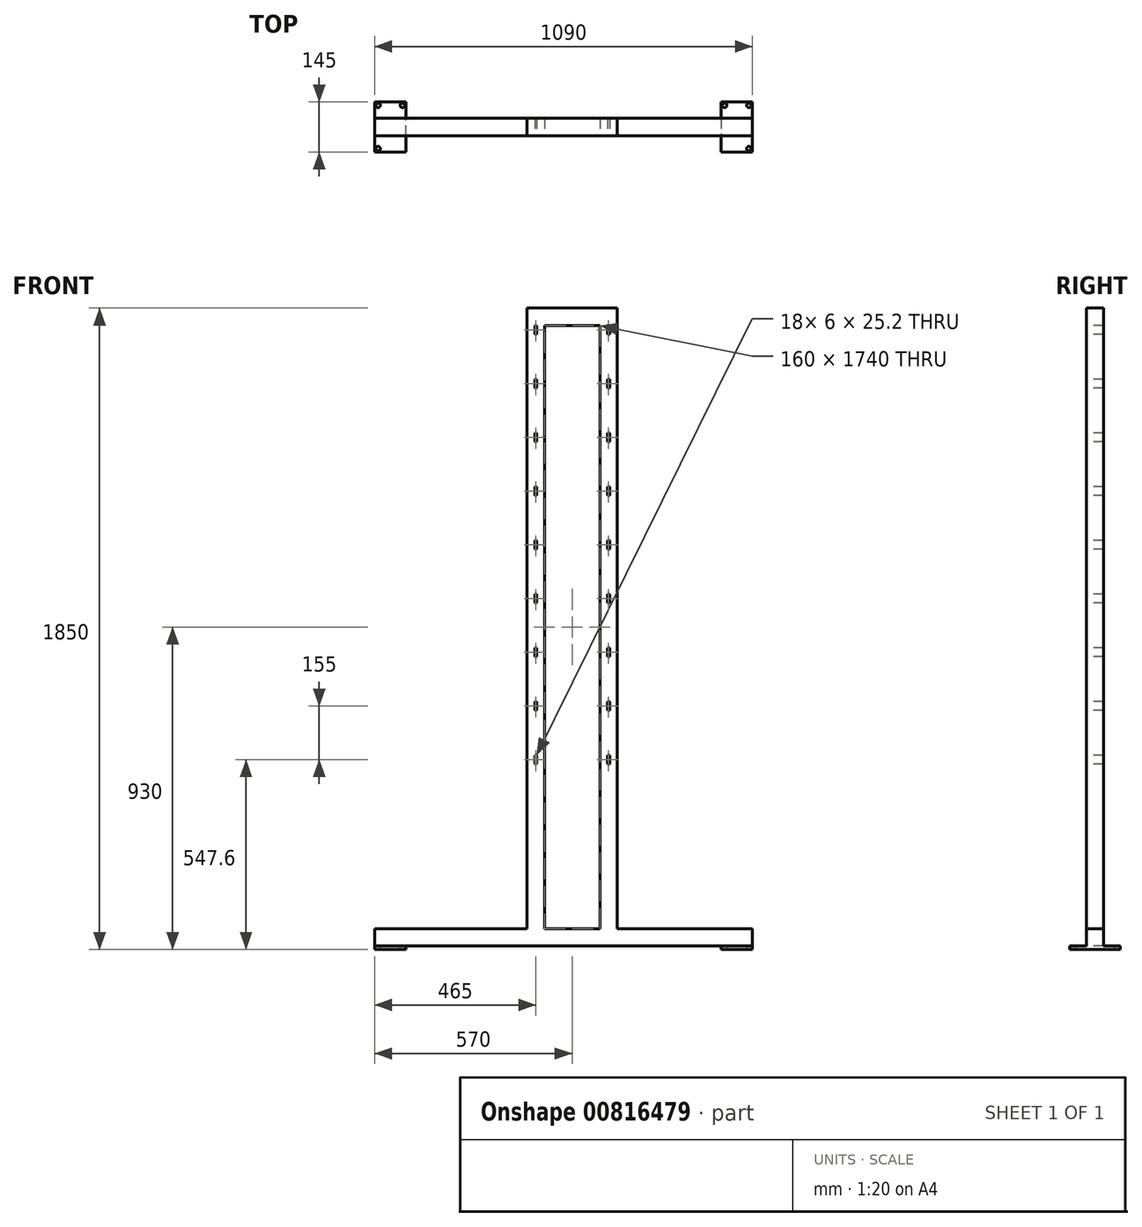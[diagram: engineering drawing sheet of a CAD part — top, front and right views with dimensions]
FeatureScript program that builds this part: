
annotation { "Feature Type Name" : "Feature", "Feature Type Description" : "" }
export const myFeature = defineFeature(function(context is Context, id is Id, definition is map)
    precondition{}
    {
        {
            var Q0;
            Q0=qCreatedBy(makeId("Top.planeOp"),FACE);
            var sketch = newSketch(context, id + "F0", { "sketchPlane" : qUnion([Q0])});
            skLineSegment(sketch, "E0.bottom", {"start": v(45, 72.5) * mm, "end": v(-45, 72.5) * mm});
            skLineSegment(sketch, "E0.top", {"start": v(45, -72.5) * mm, "end": v(-45, -72.5) * mm});
            skLineSegment(sketch, "E0.left", {"start": v(45, 72.5) * mm, "end": v(45, -72.5) * mm});
            skLineSegment(sketch, "E0.right", {"start": v(-45, 72.5) * mm, "end": v(-45, -72.5) * mm});
            skPoint(sketch, "E0.middle", {"position": v(0, 0) * mm});
            skSolve(sketch);
        }
        {
            var Q0;
            Q0=makeQuery(id+"F0.imprint","IMPRINT",FACE,{"disambiguationData":[TD([[makeQuery(id+"F0.imprint","IMPRINT",EDGE,{"derivedFrom":sQuery(id+"F0.wireOp",EDGE,"E0.bottom")}),1.0]])]});
            extrude(context, id + "F1", {"entities" : qUnion([Q0]), "depth" : 10 * mm, "offsetDistance" : 25 * mm});
        }
        {
            var Q0;
            Q0=qCreatedBy(makeId("Top.planeOp"),FACE);
            var sketch = newSketch(context, id + "F2", { "sketchPlane" : qUnion([Q0])});
            skPoint(sketch, "E1", {"position": v(35, 62.5) * mm});
            skPoint(sketch, "E2", {"position": v(35, -62.5) * mm});
            skPoint(sketch, "E3", {"position": v(-35, 62.5) * mm});
            skSolve(sketch);
        }
        {
            var Q0;
            Q0=sQuery(id+"F2.wireOp",VERTEX,"E1");
            var Q1;
            Q1=sQuery(id+"F2.wireOp",VERTEX,"E2");
            var Q2;
            Q2=sQuery(id+"F2.wireOp",VERTEX,"E3");
            var Q3;
            Q3=makeQuery(id+"F1.opExtrude","SWEPT_BODY",BODY,{"disambiguationData":[OSD([sQuery(id+"F0.wireOp",EDGE,"E0.bottom"),sQuery(id+"F0.wireOp",EDGE,"E0.top"),sQuery(id+"F0.wireOp",EDGE,"E0.left"),sQuery(id+"F0.wireOp",EDGE,"E0.right")])]});
            hole(context, id + "F3", {"style" : HoleStyle.SIMPLE, "endStyle" : HoleEndStyle.THROUGH, "oppositeDirection" : true, "standardTappedOrClearance" : lookupTablePath({ "standard" : "ISO", "fit" : "Normal", "size" : "M12", "type" : "Clearance" }), "standardBlindInLast" : lookupTablePath({ "fit" : "Standard", "standard" : "ISO", "size" : "M12", "type" : "Clearance" }), "holeDiameter" : 13.2 * mm, "majorDiameter" : 5 * mm, "isTappedThrough" : true, "tappedDepth" : 12 * mm, "tapClearance" : 3, "locations" : qUnion([Q0, Q1, Q2]), "scope" : qUnion([Q3])});
        }
        {
            var Q0;
            Q0=makeQuery(id+"F1.opExtrude","CAP_FACE",FACE,{"disambiguationData":[OSD([sQuery(id+"F0.wireOp",EDGE,"E0.bottom"),sQuery(id+"F0.wireOp",EDGE,"E0.top"),sQuery(id+"F0.wireOp",EDGE,"E0.left"),sQuery(id+"F0.wireOp",EDGE,"E0.right")])],"isStart":false});
            var sketch = newSketch(context, id + "F4", { "sketchPlane" : qUnion([Q0])});
            skLineSegment(sketch, "E4.bottom", {"start": v(45, 25) * mm, "end": v(-45, 25) * mm});
            skLineSegment(sketch, "E4.top", {"start": v(45, -25) * mm, "end": v(-45, -25) * mm});
            skLineSegment(sketch, "E4.left", {"start": v(45, 25) * mm, "end": v(45, -25) * mm});
            skLineSegment(sketch, "E4.right", {"start": v(-45, 25) * mm, "end": v(-45, -25) * mm});
            skPoint(sketch, "E4.middle", {"position": v(0, 0) * mm});
            skSolve(sketch);
        }
        {
            var Q0;
            Q0 = qSketchRegion(id + "F4", true);
            extrude(context, id + "F5", {"entities" : qUnion([Q0]), "operationType" : NewBodyOperationType.ADD, "depth" : 50 * mm, "offsetDistance" : 25 * mm});
        }
        {
            var Q0;
            Q0=makeQuery(id+"F5.boolean.opBoolean","MERGE",FACE,{"derivedFrom":[makeQuery(id+"F1.opExtrude","SWEPT_FACE",FACE,{"disambiguationData":[OSD([sQuery(id+"F0.wireOp",EDGE,"E0.right")])]}),makeQuery(id+"F5.opExtrude","SWEPT_FACE",FACE,{"disambiguationData":[OSD([sQuery(id+"F4.wireOp",EDGE,"E4.right")])]})]});
            var sketch = newSketch(context, id + "F6", { "sketchPlane" : qUnion([Q0])});
            skLineSegment(sketch, "E5.bottom", {"start": v(-25, 60) * mm, "end": v(25, 60) * mm});
            skLineSegment(sketch, "E5.top", {"start": v(-25, 10) * mm, "end": v(25, 10) * mm});
            skLineSegment(sketch, "E5.left", {"start": v(-25, 60) * mm, "end": v(-25, 10) * mm});
            skLineSegment(sketch, "E5.right", {"start": v(25, 60) * mm, "end": v(25, 10) * mm});
            skSolve(sketch);
        }
        {
            var Q0;
            Q0 = qSketchRegion(id + "F6", true);
            extrude(context, id + "F7", {"entities" : qUnion([Q0]), "operationType" : NewBodyOperationType.ADD, "depth" : 1000 * mm, "offsetDistance" : 25 * mm});
        }
        {
            var Q0;
            Q0=makeQuery(id+"F7.opExtrude","SWEPT_FACE",FACE,{"disambiguationData":[OSD([sQuery(id+"F6.wireOp",EDGE,"E5.top")])]});
            var sketch = newSketch(context, id + "F8", { "sketchPlane" : qUnion([Q0])});
            skLineSegment(sketch, "E6.bottom", {"start": v(-955, 72.5) * mm, "end": v(-1045, 72.5) * mm});
            skLineSegment(sketch, "E6.top", {"start": v(-955, -72.5) * mm, "end": v(-1045, -72.5) * mm});
            skLineSegment(sketch, "E6.left", {"start": v(-955, 72.5) * mm, "end": v(-955, -72.5) * mm});
            skLineSegment(sketch, "E6.right", {"start": v(-1045, 72.5) * mm, "end": v(-1045, -72.5) * mm});
            skPoint(sketch, "E6.middle", {"position": v(-1000, 0) * mm});
            skPoint(sketch, "E6.middle.positionSnap0", {"position": v(-1045, 0) * mm});
            skPoint(sketch, "E6.centerSnap0", {"position": v(-1045, 0) * mm});
            skSolve(sketch);
        }
        {
            var Q0;
            Q0 = qSketchRegion(id + "F8", true);
            extrude(context, id + "F9", {"entities" : qUnion([Q0]), "operationType" : NewBodyOperationType.ADD, "depth" : 10 * mm, "offsetDistance" : 25 * mm});
        }
        {
            var Q0;
            {var subQ2=sQuery(id+"F8.wireOp",EDGE,"E6.top");var subQ3=sQuery(id+"F8.wireOp",EDGE,"E6.left");var subQ4=sQuery(id+"F8.wireOp",EDGE,"E6.right");Q0=makeQuery(id+"F9.boolean.opBoolean","SPLIT",FACE,{"disambiguationData":[TD([makeQuery(id+"F5.opExtrude","SWEPT_FACE",FACE,{"disambiguationData":[OSD([sQuery(id+"F4.wireOp",EDGE,"E4.bottom")])]})])],"derivedFrom":makeQuery(id+"F9.opExtrude","CAP_FACE",FACE,{"disambiguationData":[OSD([sQuery(id+"F8.wireOp",EDGE,"E6.bottom"),subQ2,subQ3,subQ4])],"isStart":true})});}
            var sketch = newSketch(context, id + "F10", { "sketchPlane" : qUnion([Q0])});
            skPoint(sketch, "E7", {"position": v(-1035, 62.5) * mm});
            skPoint(sketch, "E8", {"position": v(-965, 62.5) * mm});
            skPoint(sketch, "E9", {"position": v(-1035, -62.5) * mm});
            skSolve(sketch);
        }
        {
            var Q0;
            Q0=sQuery(id+"F10.wireOp",VERTEX,"E8");
            var Q1;
            Q1=sQuery(id+"F10.wireOp",VERTEX,"E9");
            var Q2;
            Q2=sQuery(id+"F10.wireOp",VERTEX,"E7");
            var Q3;
            Q3=makeQuery(id+"F1.opExtrude","SWEPT_BODY",BODY,{"disambiguationData":[OSD([sQuery(id+"F0.wireOp",EDGE,"E0.bottom"),sQuery(id+"F0.wireOp",EDGE,"E0.top"),sQuery(id+"F0.wireOp",EDGE,"E0.left"),sQuery(id+"F0.wireOp",EDGE,"E0.right")])]});
            hole(context, id + "F11", {"style" : HoleStyle.SIMPLE, "endStyle" : HoleEndStyle.THROUGH, "standardTappedOrClearance" : lookupTablePath({ "standard" : "ISO", "fit" : "Normal", "size" : "M12", "type" : "Clearance" }), "standardBlindInLast" : lookupTablePath({ "fit" : "Standard", "standard" : "ISO", "size" : "M12", "type" : "Clearance" }), "holeDiameter" : 13.2 * mm, "majorDiameter" : 5 * mm, "isTappedThrough" : true, "tappedDepth" : 12 * mm, "tapClearance" : 3, "locations" : qUnion([Q0, Q1, Q2]), "scope" : qUnion([Q3])});
        }
        {
            var Q0;
            Q0=makeQuery(id+"F7.boolean.opBoolean","MERGE",FACE,{"derivedFrom":[makeQuery(id+"F5.opExtrude","CAP_FACE",FACE,{"disambiguationData":[OSD([sQuery(id+"F4.wireOp",EDGE,"E4.bottom"),sQuery(id+"F4.wireOp",EDGE,"E4.top"),sQuery(id+"F4.wireOp",EDGE,"E4.left"),sQuery(id+"F4.wireOp",EDGE,"E4.right")])],"isStart":false}),makeQuery(id+"F7.opExtrude","SWEPT_FACE",FACE,{"disambiguationData":[OSD([sQuery(id+"F6.wireOp",EDGE,"E5.bottom")])]})]});
            var sketch = newSketch(context, id + "F12", { "sketchPlane" : qUnion([Q0])});
            skLineSegment(sketch, "E10.bottom", {"start": v(-345, 25) * mm, "end": v(-395, 25) * mm});
            skLineSegment(sketch, "E10.top", {"start": v(-345, -25) * mm, "end": v(-395, -25) * mm});
            skLineSegment(sketch, "E10.left", {"start": v(-395, 25) * mm, "end": v(-395, -25) * mm});
            skLineSegment(sketch, "E10.right", {"start": v(-345, 25) * mm, "end": v(-345, -25) * mm});
            skPoint(sketch, "E10.middle", {"position": v(-370, 0) * mm});
            skPoint(sketch, "E10.middle.positionSnap0", {"position": v(45, 0) * mm});
            skPoint(sketch, "E10.centerSnap0", {"position": v(45, 0) * mm});
            skLineSegment(sketch, "E11.bottom", {"start": v(-555, 25) * mm, "end": v(-605, 25) * mm});
            skLineSegment(sketch, "E11.top", {"start": v(-555, -25) * mm, "end": v(-605, -25) * mm});
            skLineSegment(sketch, "E11.left", {"start": v(-555, 25) * mm, "end": v(-555, -25) * mm});
            skLineSegment(sketch, "E11.right", {"start": v(-605, 25) * mm, "end": v(-605, -25) * mm});
            skPoint(sketch, "E11.middle", {"position": v(-580, 0) * mm});
            skSolve(sketch);
        }
        {
            var Q0;
            Q0 = qSketchRegion(id + "F12", true);
            extrude(context, id + "F13", {"entities" : qUnion([Q0]), "operationType" : NewBodyOperationType.ADD, "depth" : 1790 * mm, "offsetDistance" : 25 * mm});
        }
        {
            var Q0;
            Q0=makeQuery(id+"F13.opExtrude","CAP_FACE",FACE,{"disambiguationData":[OSD([sQuery(id+"F12.wireOp",EDGE,"E11.bottom"),sQuery(id+"F12.wireOp",EDGE,"E11.top"),sQuery(id+"F12.wireOp",EDGE,"E11.left"),sQuery(id+"F12.wireOp",EDGE,"E11.right")])],"isStart":false});
            var sketch = newSketch(context, id + "F14", { "sketchPlane" : qUnion([Q0])});
            skLineSegment(sketch, "E12.bottom", {"start": v(-605, 25) * mm, "end": v(-345, 25) * mm});
            skLineSegment(sketch, "E12.top", {"start": v(-605, -25) * mm, "end": v(-345, -25) * mm});
            skLineSegment(sketch, "E12.left", {"start": v(-605, 25) * mm, "end": v(-605, -25) * mm});
            skLineSegment(sketch, "E12.right", {"start": v(-345, 25) * mm, "end": v(-345, -25) * mm});
            skSolve(sketch);
        }
        {
            var Q0;
            Q0 = qSketchRegion(id + "F14", true);
            extrude(context, id + "F15", {"entities" : qUnion([Q0]), "operationType" : NewBodyOperationType.ADD, "oppositeDirection" : true, "depth" : 50 * mm, "offsetDistance" : 25 * mm});
        }
        {
            var Q0;
            Q0=makeQuery(id+"F15.boolean.opBoolean","MERGE",FACE,{"derivedFrom":[makeQuery(id+"F13.boolean.opBoolean","MERGE",FACE,{"derivedFrom":[makeQuery(id+"F7.boolean.opBoolean","MERGE",FACE,{"derivedFrom":[makeQuery(id+"F5.opExtrude","SWEPT_FACE",FACE,{"disambiguationData":[OSD([sQuery(id+"F4.wireOp",EDGE,"E4.top")])]}),makeQuery(id+"F7.opExtrude","SWEPT_FACE",FACE,{"disambiguationData":[OSD([sQuery(id+"F6.wireOp",EDGE,"E5.right")])]})]}),makeQuery(id+"F13.opExtrude","SWEPT_FACE",FACE,{"disambiguationData":[OSD([sQuery(id+"F12.wireOp",EDGE,"E10.top")])]}),makeQuery(id+"F13.opExtrude","SWEPT_FACE",FACE,{"disambiguationData":[OSD([sQuery(id+"F12.wireOp",EDGE,"E11.top")])]})]}),makeQuery(id+"F15.opExtrude","SWEPT_FACE",FACE,{"disambiguationData":[OSD([sQuery(id+"F14.wireOp",EDGE,"E12.top")])]})]});
            var sketch = newSketch(context, id + "F16", { "sketchPlane" : qUnion([Q0])});
            skLineSegment(sketch, "E13.bottom", {"start": v(-367, 535) * mm, "end": v(-373, 535) * mm});
            skLineSegment(sketch, "E13.top", {"start": v(-367, 560.2) * mm, "end": v(-373, 560.2) * mm});
            skLineSegment(sketch, "E13.left", {"start": v(-367, 535) * mm, "end": v(-367, 560.2) * mm});
            skLineSegment(sketch, "E13.right", {"start": v(-373, 535) * mm, "end": v(-373, 560.2) * mm});
            skPoint(sketch, "E13.middle", {"position": v(-370, 547.6) * mm});
            skPoint(sketch, "E14.0.1.0", {"position": v(-370, 702.6) * mm});
            skLineSegment(sketch, "E14.direction1", {"start": v(-370, 547.6) * mm, "end": v(-370, 547.6) * mm});
            skLineSegment(sketch, "E15.0.1.0", {"start": v(-373, 690) * mm, "end": v(-373, 715.2) * mm});
            skLineSegment(sketch, "E15.0.1.1", {"start": v(-367, 715.2) * mm, "end": v(-373, 715.2) * mm});
            skLineSegment(sketch, "E15.0.1.2", {"start": v(-367, 690) * mm, "end": v(-367, 715.2) * mm});
            skLineSegment(sketch, "E15.0.1.3", {"start": v(-367, 690) * mm, "end": v(-373, 690) * mm});
            skLineSegment(sketch, "E15.0.2.0", {"start": v(-373, 845) * mm, "end": v(-373, 870.2) * mm});
            skLineSegment(sketch, "E15.0.2.1", {"start": v(-367, 870.2) * mm, "end": v(-373, 870.2) * mm});
            skLineSegment(sketch, "E15.0.2.2", {"start": v(-367, 845) * mm, "end": v(-367, 870.2) * mm});
            skLineSegment(sketch, "E15.0.2.3", {"start": v(-367, 845) * mm, "end": v(-373, 845) * mm});
            skLineSegment(sketch, "E15.0.3.0", {"start": v(-373, 1000) * mm, "end": v(-373, 1025.2) * mm});
            skLineSegment(sketch, "E15.0.3.1", {"start": v(-367, 1025.2) * mm, "end": v(-373, 1025.2) * mm});
            skLineSegment(sketch, "E15.0.3.2", {"start": v(-367, 1000) * mm, "end": v(-367, 1025.2) * mm});
            skLineSegment(sketch, "E15.0.3.3", {"start": v(-367, 1000) * mm, "end": v(-373, 1000) * mm});
            skLineSegment(sketch, "E15.0.4.0", {"start": v(-373, 1155) * mm, "end": v(-373, 1180.2) * mm});
            skLineSegment(sketch, "E15.0.4.1", {"start": v(-367, 1180.2) * mm, "end": v(-373, 1180.2) * mm});
            skLineSegment(sketch, "E15.0.4.2", {"start": v(-367, 1155) * mm, "end": v(-367, 1180.2) * mm});
            skLineSegment(sketch, "E15.0.4.3", {"start": v(-367, 1155) * mm, "end": v(-373, 1155) * mm});
            skLineSegment(sketch, "E15.direction1", {"start": v(-373, 535) * mm, "end": v(-373, 535) * mm});
            skLineSegment(sketch, "E15.direction2", {"start": v(-373, 535) * mm, "end": v(-373, 690) * mm, "construction": true});
            skLineSegment(sketch, "E16.0.0.5", {"start": v(-373, 1310) * mm, "end": v(-373, 1335.2) * mm});
            skLineSegment(sketch, "E16.3.0.5", {"start": v(-367, 1335.2) * mm, "end": v(-373, 1335.2) * mm});
            skLineSegment(sketch, "E16.6.0.5", {"start": v(-367, 1310) * mm, "end": v(-367, 1335.2) * mm});
            skLineSegment(sketch, "E16.9.0.5", {"start": v(-367, 1310) * mm, "end": v(-373, 1310) * mm});
            skLineSegment(sketch, "E16.0.0.6", {"start": v(-373, 1465) * mm, "end": v(-373, 1490.2) * mm});
            skLineSegment(sketch, "E16.3.0.6", {"start": v(-367, 1490.2) * mm, "end": v(-373, 1490.2) * mm});
            skLineSegment(sketch, "E16.6.0.6", {"start": v(-367, 1465) * mm, "end": v(-367, 1490.2) * mm});
            skLineSegment(sketch, "E16.9.0.6", {"start": v(-367, 1465) * mm, "end": v(-373, 1465) * mm});
            skLineSegment(sketch, "E16.0.0.7", {"start": v(-373, 1620) * mm, "end": v(-373, 1645.2) * mm});
            skLineSegment(sketch, "E16.3.0.7", {"start": v(-367, 1645.2) * mm, "end": v(-373, 1645.2) * mm});
            skLineSegment(sketch, "E16.6.0.7", {"start": v(-367, 1620) * mm, "end": v(-367, 1645.2) * mm});
            skLineSegment(sketch, "E16.9.0.7", {"start": v(-367, 1620) * mm, "end": v(-373, 1620) * mm});
            skLineSegment(sketch, "E16.0.0.8", {"start": v(-373, 1775) * mm, "end": v(-373, 1800.2) * mm});
            skLineSegment(sketch, "E16.3.0.8", {"start": v(-367, 1800.2) * mm, "end": v(-373, 1800.2) * mm});
            skLineSegment(sketch, "E16.6.0.8", {"start": v(-367, 1775) * mm, "end": v(-367, 1800.2) * mm});
            skLineSegment(sketch, "E16.9.0.8", {"start": v(-367, 1775) * mm, "end": v(-373, 1775) * mm});
            skLineSegment(sketch, "E17.bottom", {"start": v(-577, 560.2) * mm, "end": v(-583, 560.2) * mm});
            skLineSegment(sketch, "E17.top", {"start": v(-577, 535) * mm, "end": v(-583, 535) * mm});
            skLineSegment(sketch, "E17.left", {"start": v(-577, 560.2) * mm, "end": v(-577, 535) * mm});
            skLineSegment(sketch, "E17.right", {"start": v(-583, 560.2) * mm, "end": v(-583, 535) * mm});
            skPoint(sketch, "E17.middle", {"position": v(-580, 547.6) * mm});
            skLineSegment(sketch, "E18.0.1.0", {"start": v(-577, 715.2) * mm, "end": v(-577, 690) * mm});
            skLineSegment(sketch, "E18.0.1.1", {"start": v(-577, 715.2) * mm, "end": v(-583, 715.2) * mm});
            skLineSegment(sketch, "E18.0.1.2", {"start": v(-583, 715.2) * mm, "end": v(-583, 690) * mm});
            skLineSegment(sketch, "E18.0.1.3", {"start": v(-577, 690) * mm, "end": v(-583, 690) * mm});
            skLineSegment(sketch, "E18.0.2.0", {"start": v(-577, 870.2) * mm, "end": v(-577, 845) * mm});
            skLineSegment(sketch, "E18.0.2.1", {"start": v(-577, 870.2) * mm, "end": v(-583, 870.2) * mm});
            skLineSegment(sketch, "E18.0.2.2", {"start": v(-583, 870.2) * mm, "end": v(-583, 845) * mm});
            skLineSegment(sketch, "E18.0.2.3", {"start": v(-577, 845) * mm, "end": v(-583, 845) * mm});
            skLineSegment(sketch, "E18.0.3.0", {"start": v(-577, 1025.2) * mm, "end": v(-577, 1000) * mm});
            skLineSegment(sketch, "E18.0.3.1", {"start": v(-577, 1025.2) * mm, "end": v(-583, 1025.2) * mm});
            skLineSegment(sketch, "E18.0.3.2", {"start": v(-583, 1025.2) * mm, "end": v(-583, 1000) * mm});
            skLineSegment(sketch, "E18.0.3.3", {"start": v(-577, 1000) * mm, "end": v(-583, 1000) * mm});
            skLineSegment(sketch, "E18.0.4.0", {"start": v(-577, 1180.2) * mm, "end": v(-577, 1155) * mm});
            skLineSegment(sketch, "E18.0.4.1", {"start": v(-577, 1180.2) * mm, "end": v(-583, 1180.2) * mm});
            skLineSegment(sketch, "E18.0.4.2", {"start": v(-583, 1180.2) * mm, "end": v(-583, 1155) * mm});
            skLineSegment(sketch, "E18.0.4.3", {"start": v(-577, 1155) * mm, "end": v(-583, 1155) * mm});
            skLineSegment(sketch, "E18.0.5.0", {"start": v(-577, 1335.2) * mm, "end": v(-577, 1310) * mm});
            skLineSegment(sketch, "E18.0.5.1", {"start": v(-577, 1335.2) * mm, "end": v(-583, 1335.2) * mm});
            skLineSegment(sketch, "E18.0.5.2", {"start": v(-583, 1335.2) * mm, "end": v(-583, 1310) * mm});
            skLineSegment(sketch, "E18.0.5.3", {"start": v(-577, 1310) * mm, "end": v(-583, 1310) * mm});
            skLineSegment(sketch, "E18.0.6.0", {"start": v(-577, 1490.2) * mm, "end": v(-577, 1465) * mm});
            skLineSegment(sketch, "E18.0.6.1", {"start": v(-577, 1490.2) * mm, "end": v(-583, 1490.2) * mm});
            skLineSegment(sketch, "E18.0.6.2", {"start": v(-583, 1490.2) * mm, "end": v(-583, 1465) * mm});
            skLineSegment(sketch, "E18.0.6.3", {"start": v(-577, 1465) * mm, "end": v(-583, 1465) * mm});
            skLineSegment(sketch, "E18.0.7.0", {"start": v(-577, 1645.2) * mm, "end": v(-577, 1620) * mm});
            skLineSegment(sketch, "E18.0.7.1", {"start": v(-577, 1645.2) * mm, "end": v(-583, 1645.2) * mm});
            skLineSegment(sketch, "E18.0.7.2", {"start": v(-583, 1645.2) * mm, "end": v(-583, 1620) * mm});
            skLineSegment(sketch, "E18.0.7.3", {"start": v(-577, 1620) * mm, "end": v(-583, 1620) * mm});
            skLineSegment(sketch, "E18.0.8.0", {"start": v(-577, 1800.2) * mm, "end": v(-577, 1775) * mm});
            skLineSegment(sketch, "E18.0.8.1", {"start": v(-577, 1800.2) * mm, "end": v(-583, 1800.2) * mm});
            skLineSegment(sketch, "E18.0.8.2", {"start": v(-583, 1800.2) * mm, "end": v(-583, 1775) * mm});
            skLineSegment(sketch, "E18.0.8.3", {"start": v(-577, 1775) * mm, "end": v(-583, 1775) * mm});
            skLineSegment(sketch, "E18.direction1", {"start": v(-577, 535) * mm, "end": v(-577, 535) * mm});
            skLineSegment(sketch, "E18.direction2", {"start": v(-577, 535) * mm, "end": v(-577, 690) * mm, "construction": true});
            skSolve(sketch);
        }
        {
            var Q0;
            Q0 = qSketchRegion(id + "F16", true);
            extrude(context, id + "F17", {"entities" : qUnion([Q0]), "operationType" : NewBodyOperationType.REMOVE, "endBound" : BoundingType.THROUGH_ALL, "oppositeDirection" : true, "depth" : 25 * mm, "offsetDistance" : 25 * mm});
        }
    });
